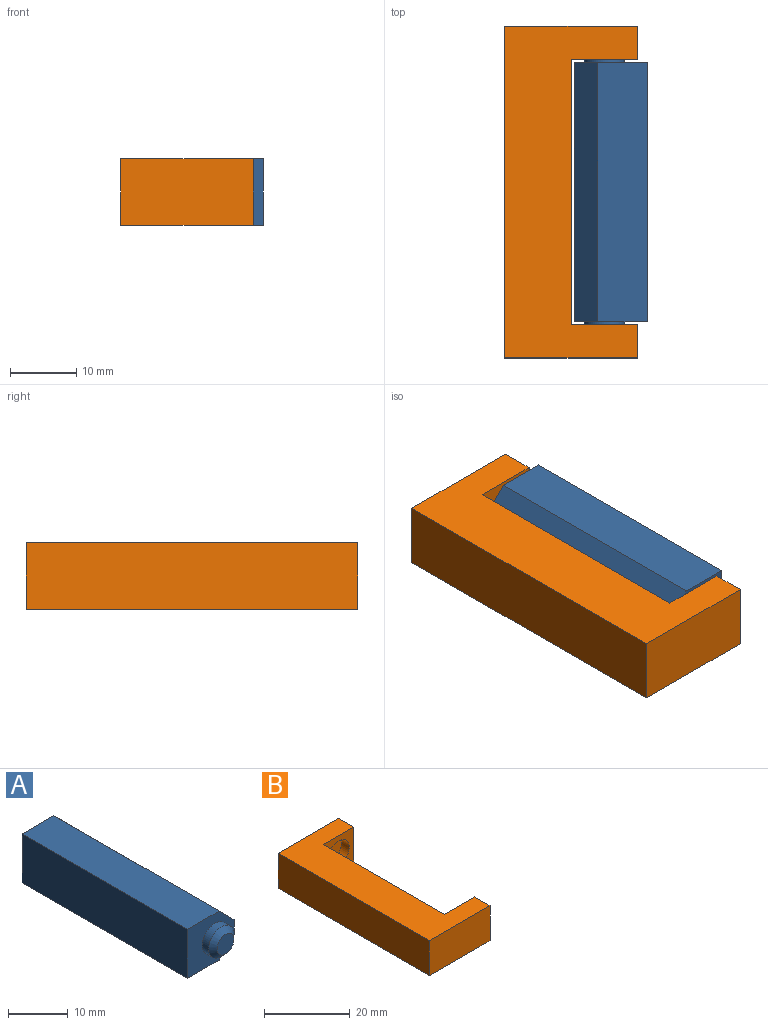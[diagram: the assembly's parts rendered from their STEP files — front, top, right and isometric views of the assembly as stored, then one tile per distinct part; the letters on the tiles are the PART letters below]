
ASSEMBLY  parts=2 mates=1
PART A: 14 faces, bbox 11x44x10 mm
  f0: plane 39x10mm, normal (-1,0,0), area 390mm2, adj f1,f3,f4,f5
  f1: plane 39x7.5mm, normal (0,0,-1), area 292.5mm2, adj f0,f4,f5,f12
  f2: plane 39x3mm, normal (1,0,0), area 117mm2, adj f4,f5,f12,f13
  f3: plane 39x7.5mm, normal (0,0,1), area 292.5mm2, adj f0,f4,f5,f13
  f4: plane 11x10mm, normal (0,-1,0), area 69.5mm2, adj f0,f1,f2,f3,f6,f12,f13
  f5: plane 11x10mm, normal (0,1,0), area 69.5mm2, adj f0,f1,f2,f3,f8,f12,f13
  f6: cylinder r=3mm len=6mm, axis (0,1,0), area 28.3mm2, adj f4,f10
  f7: plane 4x4mm, normal (0,-1,0), area 12.6mm2, adj f10
  f8: cylinder r=3mm len=6mm, axis (0,-1,0), area 28.3mm2, adj f5,f11
  f9: plane 4x4mm, normal (0,1,0), area 12.6mm2, adj f11
  f10: cone r=2mm half-angle=45deg, axis (0,1,0), area 22.2mm2, adj f6,f7
  f11: cone r=2mm half-angle=45deg, axis (0,-1,0), area 22.2mm2, adj f8,f9
  f12: plane 39x3.5mm, normal (0.71,0,-0.71), area 193mm2, adj f1,f2,f4,f5
  f13: plane 39x3.5mm, normal (0.71,0,0.71), area 193mm2, adj f2,f3,f4,f5
PART B: 14 faces, bbox 20x50x10 mm
  f0: plane 20x10mm, normal (0,-1,0), area 200mm2, adj f1,f7,f8,f9
  f1: plane 10x5mm, normal (1,0,0), area 50mm2, adj f0,f2,f8,f9
  f2: plane 10x10mm, normal (0,1,0), area 61.5mm2, adj f1,f3,f8,f9,f12
  f3: plane 40x10mm, normal (1,0,0), area 400mm2, adj f2,f4,f8,f9
  f4: plane 10x10mm, normal (0,-1,0), area 61.5mm2, adj f3,f5,f8,f9,f10
  f5: plane 10x5mm, normal (1,0,0), area 50mm2, adj f4,f6,f8,f9
  f6: plane 20x10mm, normal (0,1,0), area 200mm2, adj f5,f7,f8,f9
  f7: plane 50x10mm, normal (-1,0,0), area 500mm2, adj f0,f6,f8,f9
  f8: plane 50x20mm, normal (0,0,1), area 600mm2, adj f0,f1,f2,f3,f4,f5,f6,f7
  f9: plane 50x20mm, normal (0,0,-1), area 600mm2, adj f0,f1,f2,f3,f4,f5,f6,f7
  f10: cylinder r=3.5mm len=7mm, axis (0,-1,0), area 55mm2, adj f4,f11
  f11: plane 7x7mm, normal (0,-1,0), area 38.5mm2, adj f10
  f12: cylinder r=3.5mm len=7mm, axis (0,1,0), area 55mm2, adj f2,f13
  f13: plane 7x7mm, normal (0,1,0), area 38.5mm2, adj f12
PLACE A rot(axis=(0,1,0),180deg) t=(10.81,-25.26,6.4)mm
PLACE B rot(axis=(0,-1,0),0deg) t=(-10.69,-69.73,-3.6)mm
MATE cylindrical B.f10 <-> A.f6  axis (0,-1,0) through (4.31,-22.23,1.4)mm
